# Revit family: FU_Sandler_Wudi 5-1
name_source: partatom
category: Furniture
units: mm (PartAtom-declared; Revit-internal decimal feet)

## family parameters
Always vertical = Yes
Cut with Voids When Loaded = No
Enable Cutting in Views = No
OmniClass Number = 23.40.20.00
OmniClass Title = General Furniture and Specialties
Render Appearance Source = Family Geometry
Room Calculation Point = No
Shared = No
Work Plane-Based = No

## types (2) — shared parameters
Depth = 770 mm  [stored 2.52625 ft]
Height = 745 mm  [stored 2.44423 ft]
Manufacturer = Sandler
URL = https://www.sandlerseating.com
Wudi Upholstery = Camira Manhatten Lexington YI113
Wudi Wood = Wood - Oak - Sandler - Walnut - Legs
zero-valued in all types: Default Elevation

## per-type parameters (varying)
| type | BS1 Extrusion End | BS1 Extrusion Start | BS2 Extrusion End | BS2 Extrusion Start | BS2 Visibility | Description | Width |
| Wudi 5.1 | 175 mm  [stored 0.574147 ft] | -175 mm  [stored -0.574147 ft] | 175 mm  [stored 0.574147 ft] | -175 mm  [stored -0.574147 ft] | No | Upholstered armchair with solid oak frame. | 755 mm  [stored 2.47703 ft] |
| Wudi 7.1 | 450 mm  [stored 1.47638 ft] | 100 mm  [stored 0.328084 ft] | -450 mm  [stored -1.47638 ft] | -100 mm  [stored -0.328084 ft] | Yes | Upholstered sofa with solid oak frame. | 1360 mm  [stored 4.46194 ft] |

note: column(s) folded — value = type name in every type: Model

note: [stored X ft] marks values corroborated as IEEE doubles in the binary element streams (Revit-internal decimal feet)

## geometry (parser evidence)
native form markers: Extrusion x4, Sweep x3
no freeform markers — native parametric forms only
